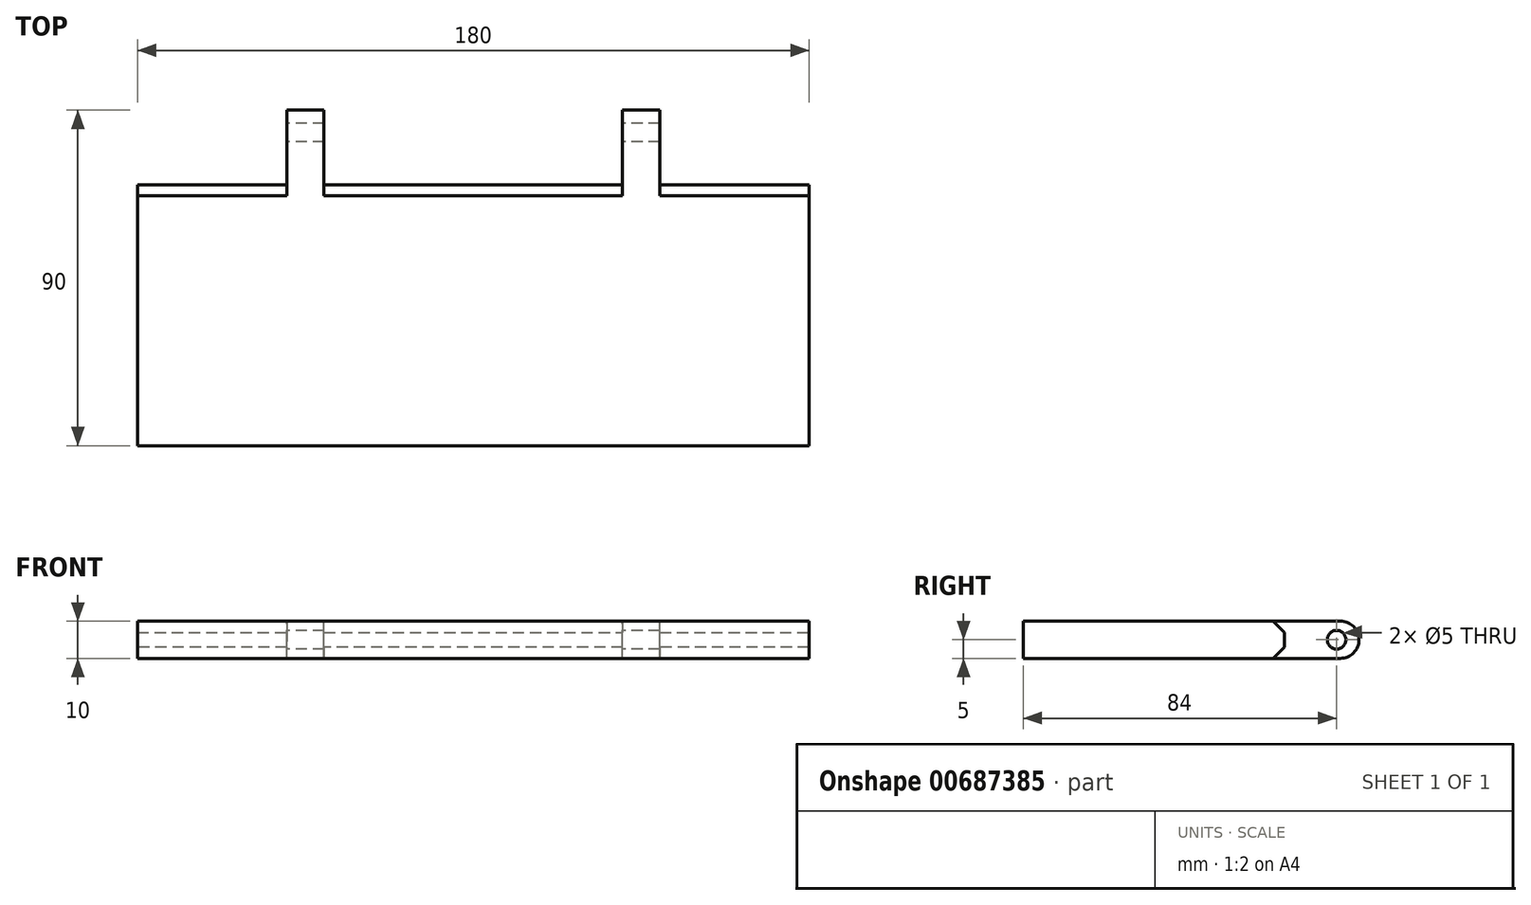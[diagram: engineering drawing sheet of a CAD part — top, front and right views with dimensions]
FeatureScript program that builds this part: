
annotation { "Feature Type Name" : "Feature", "Feature Type Description" : "" }
export const myFeature = defineFeature(function(context is Context, id is Id, definition is map)
    precondition{}
    {
        {
            var Q0;
            Q0=qCreatedBy(makeId("Top.planeOp"),FACE);
            var sketch = newSketch(context, id + "F0", { "sketchPlane" : qUnion([Q0])});
            skLineSegment(sketch, "E0.bottom", {"start": v(0, 0) * mm, "end": v(180, 0) * mm});
            skLineSegment(sketch, "E0.top", {"start": v(0, 70) * mm, "end": v(180, 70) * mm});
            skLineSegment(sketch, "E0.left", {"start": v(0, 0) * mm, "end": v(0, 70) * mm});
            skLineSegment(sketch, "E0.right", {"start": v(180, 0) * mm, "end": v(180, 70) * mm});
            skSolve(sketch);
        }
        {
            var Q0;
            Q0=makeQuery(id+"F0.imprint","IMPRINT",FACE,{"disambiguationData":[TD([[makeQuery(id+"F0.imprint","IMPRINT",EDGE,{"derivedFrom":sQuery(id+"F0.wireOp",EDGE,"E0.bottom")}),1.0]])]});
            extrude(context, id + "F1", {"entities" : qUnion([Q0]), "depth" : 10 * mm, "offsetDistance" : 25 * mm});
        }
        {
            var Q0;
            Q0=makeQuery(id+"F1.opExtrude","SWEPT_FACE",FACE,{"disambiguationData":[OSD([sQuery(id+"F0.wireOp",EDGE,"E0.top")])]});
            var sketch = newSketch(context, id + "F2", { "sketchPlane" : qUnion([Q0])});
            skLineSegment(sketch, "E1", {"start": v(-90, 0) * mm, "end": v(-90, 10) * mm, "construction": true});
            skPoint(sketch, "E2", {"position": v(-90, 0) * mm});
            skPoint(sketch, "E3", {"position": v(-90, 10) * mm});
            skLineSegment(sketch, "E4", {"start": v(-90, 0) * mm, "end": v(-180, 0) * mm, "construction": true});
            skLineSegment(sketch, "E5", {"start": v(-180, 0) * mm, "end": v(-135, 0) * mm, "construction": true});
            skLineSegment(sketch, "E6", {"start": v(-135, 0) * mm, "end": v(-135, 10) * mm, "construction": true});
            skLineSegment(sketch, "E7.MirrorCS", {"start": v(-90, 0) * mm, "end": v(0, 0) * mm, "construction": true});
            skLineSegment(sketch, "E8.MirrorCS", {"start": v(-45, 0) * mm, "end": v(-45, 10) * mm, "construction": true});
            skPoint(sketch, "E9", {"position": v(-45, 5) * mm});
            skPoint(sketch, "E10", {"position": v(-135, 5) * mm});
            skPoint(sketch, "E11", {"position": v(-90, 5) * mm});
            skSolve(sketch);
        }
        {
            var Q0;
            {var subQ0=sQuery(id+"F0.wireOp",EDGE,"E0.top");Q0=makeQuery(id+"F2.imprint","IMPRINT",FACE,{"disambiguationData":[TD([[makeQuery(id+"F2.imprint","IMPRINT",EDGE,{"derivedFrom":makeQuery(id+"F1.opExtrude","CAP_EDGE",EDGE,{"disambiguationData":[OSD([subQ0])],"isStart":true})}),-1.0]])]});}
            var sketch = newSketch(context, id + "F3", { "sketchPlane" : qUnion([Q0])});
            skLineSegment(sketch, "E12.bottom", {"start": v(-130, 0) * mm, "end": v(-140, 0) * mm});
            skLineSegment(sketch, "E12.top", {"start": v(-130, 10) * mm, "end": v(-140, 10) * mm});
            skLineSegment(sketch, "E12.left", {"start": v(-130, 0) * mm, "end": v(-130, 10) * mm});
            skLineSegment(sketch, "E12.right", {"start": v(-140, 0) * mm, "end": v(-140, 10) * mm});
            skPoint(sketch, "E12.middle", {"position": v(-135, 5) * mm});
            skLineSegment(sketch, "E13.MirrorCS", {"start": v(-50, 0) * mm, "end": v(-50, 10) * mm});
            skLineSegment(sketch, "E14.MirrorCS", {"start": v(-50, 10) * mm, "end": v(-40, 10) * mm});
            skLineSegment(sketch, "E15.MirrorCS", {"start": v(-40, 0) * mm, "end": v(-40, 10) * mm});
            skLineSegment(sketch, "E16.MirrorCS", {"start": v(-50, 0) * mm, "end": v(-40, 0) * mm});
            skPoint(sketch, "E17.MirrorP", {"position": v(-45, 5) * mm});
            skSolve(sketch);
        }
        {
            var Q0;
            Q0 = qSketchRegion(id + "F3", true);
            extrude(context, id + "F4", {"entities" : qUnion([Q0]), "operationType" : NewBodyOperationType.ADD, "depth" : 20 * mm, "offsetDistance" : 25 * mm});
        }
        {
            var Q0;
            Q0=makeQuery(id+"F4.opExtrude","SWEPT_FACE",FACE,{"disambiguationData":[OSD([sQuery(id+"F3.wireOp",EDGE,"E15.MirrorCS")])]});
            var sketch = newSketch(context, id + "F5", { "sketchPlane" : qUnion([Q0])});
            skCircle(sketch, "E18", {"center": v(-84, 5) * mm, "radius": 2.5 * mm});
            skPoint(sketch, "E18.centerSnap0", {"position": v(-70, 5) * mm});
            skPoint(sketch, "E18.centerSnap1", {"position": v(-84, 10) * mm});
            skSolve(sketch);
        }
        {
            var Q0;
            Q0=makeQuery(id+"F5.imprint","IMPRINT",FACE,{"disambiguationData":[TD([[makeQuery(id+"F5.imprint","IMPRINT",EDGE,{"derivedFrom":sQuery(id+"F5.wireOp",EDGE,"E18")}),1.0]])]});
            extrude(context, id + "F6", {"entities" : qUnion([Q0]), "operationType" : NewBodyOperationType.REMOVE, "endBound" : BoundingType.THROUGH_ALL, "oppositeDirection" : true, "depth" : 25 * mm, "offsetDistance" : 25 * mm});
        }
        {
            var Q0;
            Q0=makeQuery(id+"F4.opExtrude","CAP_EDGE",EDGE,{"disambiguationData":[OSD([sQuery(id+"F3.wireOp",EDGE,"E12.top")])],"isStart":false});
            var Q1;
            Q1=makeQuery(id+"F4.opExtrude","CAP_EDGE",EDGE,{"disambiguationData":[OSD([sQuery(id+"F3.wireOp",EDGE,"E12.bottom")])],"isStart":false});
            var Q2;
            Q2=makeQuery(id+"F4.opExtrude","CAP_EDGE",EDGE,{"disambiguationData":[OSD([sQuery(id+"F3.wireOp",EDGE,"E16.MirrorCS")])],"isStart":false});
            var Q3;
            Q3=makeQuery(id+"F4.opExtrude","CAP_EDGE",EDGE,{"disambiguationData":[OSD([sQuery(id+"F3.wireOp",EDGE,"E14.MirrorCS")])],"isStart":false});
            fillet(context, id + "F7", {"entities" : qUnion([Q0, Q1, Q2, Q3]), "radius" : 5 * mm, "tangentPropagation" : true, "allowEdgeOverflow" : false});
        }
        {
            var Q0;
            {var subQ0=sQuery(id+"F0.wireOp",EDGE,"E0.top");Q0=makeQuery(id+"F4.boolean.opBoolean","SPLIT",EDGE,{"disambiguationData":[TD([makeQuery(id+"F4.opExtrude","SWEPT_FACE",FACE,{"disambiguationData":[OSD([sQuery(id+"F3.wireOp",EDGE,"E12.left")])]})])],"derivedFrom":makeQuery(id+"F1.opExtrude","CAP_EDGE",EDGE,{"disambiguationData":[OSD([subQ0])],"isStart":false})});}
            var Q1;
            {var subQ0=sQuery(id+"F0.wireOp",EDGE,"E0.left");var subQ1=sQuery(id+"F0.wireOp",EDGE,"E0.top");Q1=makeQuery(id+"F4.boolean.opBoolean","SPLIT",EDGE,{"disambiguationData":[TD([makeQuery(id+"F1.opExtrude","SWEPT_FACE",FACE,{"disambiguationData":[OSD([subQ0])]})])],"derivedFrom":makeQuery(id+"F1.opExtrude","CAP_EDGE",EDGE,{"disambiguationData":[OSD([subQ1])],"isStart":false})});}
            var Q2;
            {var subQ0=sQuery(id+"F0.wireOp",EDGE,"E0.right");var subQ1=sQuery(id+"F0.wireOp",EDGE,"E0.top");Q2=makeQuery(id+"F4.boolean.opBoolean","SPLIT",EDGE,{"disambiguationData":[TD([makeQuery(id+"F1.opExtrude","SWEPT_FACE",FACE,{"disambiguationData":[OSD([subQ0])]})])],"derivedFrom":makeQuery(id+"F1.opExtrude","CAP_EDGE",EDGE,{"disambiguationData":[OSD([subQ1])],"isStart":false})});}
            var Q3;
            {var subQ0=sQuery(id+"F0.wireOp",EDGE,"E0.right");var subQ1=sQuery(id+"F0.wireOp",EDGE,"E0.top");Q3=makeQuery(id+"F4.boolean.opBoolean","SPLIT",EDGE,{"disambiguationData":[TD([makeQuery(id+"F1.opExtrude","SWEPT_FACE",FACE,{"disambiguationData":[OSD([subQ0])]})])],"derivedFrom":makeQuery(id+"F1.opExtrude","CAP_EDGE",EDGE,{"disambiguationData":[OSD([subQ1])],"isStart":true})});}
            var Q4;
            {var subQ0=sQuery(id+"F0.wireOp",EDGE,"E0.top");Q4=makeQuery(id+"F4.boolean.opBoolean","SPLIT",EDGE,{"disambiguationData":[TD([makeQuery(id+"F4.opExtrude","SWEPT_FACE",FACE,{"disambiguationData":[OSD([sQuery(id+"F3.wireOp",EDGE,"E12.left")])]})])],"derivedFrom":makeQuery(id+"F1.opExtrude","CAP_EDGE",EDGE,{"disambiguationData":[OSD([subQ0])],"isStart":true})});}
            var Q5;
            {var subQ0=sQuery(id+"F0.wireOp",EDGE,"E0.left");var subQ1=sQuery(id+"F0.wireOp",EDGE,"E0.top");Q5=makeQuery(id+"F4.boolean.opBoolean","SPLIT",EDGE,{"disambiguationData":[TD([makeQuery(id+"F1.opExtrude","SWEPT_FACE",FACE,{"disambiguationData":[OSD([subQ0])]})])],"derivedFrom":makeQuery(id+"F1.opExtrude","CAP_EDGE",EDGE,{"disambiguationData":[OSD([subQ1])],"isStart":true})});}
            chamfer(context, id + "F8", {"entities" : qUnion([Q0, Q1, Q2, Q3, Q4, Q5]), "width" : 3 * mm, "tangentPropagation" : true});
        }
    });
